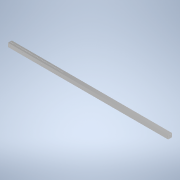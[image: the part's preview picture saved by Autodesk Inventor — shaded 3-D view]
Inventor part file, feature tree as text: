
AUTODESK INVENTOR PART (.ipt)
format: ipt  version: 2020.3 (Build 243373000, 373)  size: 285,696 bytes
history: native  units: mm
features: sketch x11, hole x8, extrude x3, other x1
ambient origin geometry x8: Origin, YZ Plane, XZ Plane, XY Plane, X Axis, Y Axis, Z Axis, Center Point
bodies: Body1 (feature_tree)
feature tree (23):
  other  "ソリッド1"
  extrude  "押し出し1"  Depth=15.0mm
  hole  "穴1"  [1 undecoded]
  hole  "穴2"  [1 undecoded]
  hole  "穴3"  [1 undecoded]
  extrude  "押し出し2"  Depth=1.2mm
  hole  "穴4"  [1 undecoded]
  hole  "穴5"  [1 undecoded]
  hole  "穴6"  [1 undecoded]
  hole  "穴7"  [1 undecoded]
  extrude  "押し出し3"  Depth=7.5mm
  hole  "穴8"  [1 undecoded]
  sketch  "スケッチ1"
  sketch  "スケッチ2"
  sketch  "スケッチ3"
  sketch  "スケッチ4"
  sketch  "スケッチ5"
  sketch  "スケッチ6"
  sketch  "スケッチ7"
  sketch  "スケッチ8"
  sketch  "スケッチ9"
  sketch  "スケッチ11"
  sketch  "スケッチ12"
note: 8 required parameter values undecoded (feature->parameter linkage not recoverable at this tier; creation-order binding heuristic only, values carry confidence <= 0.55)
